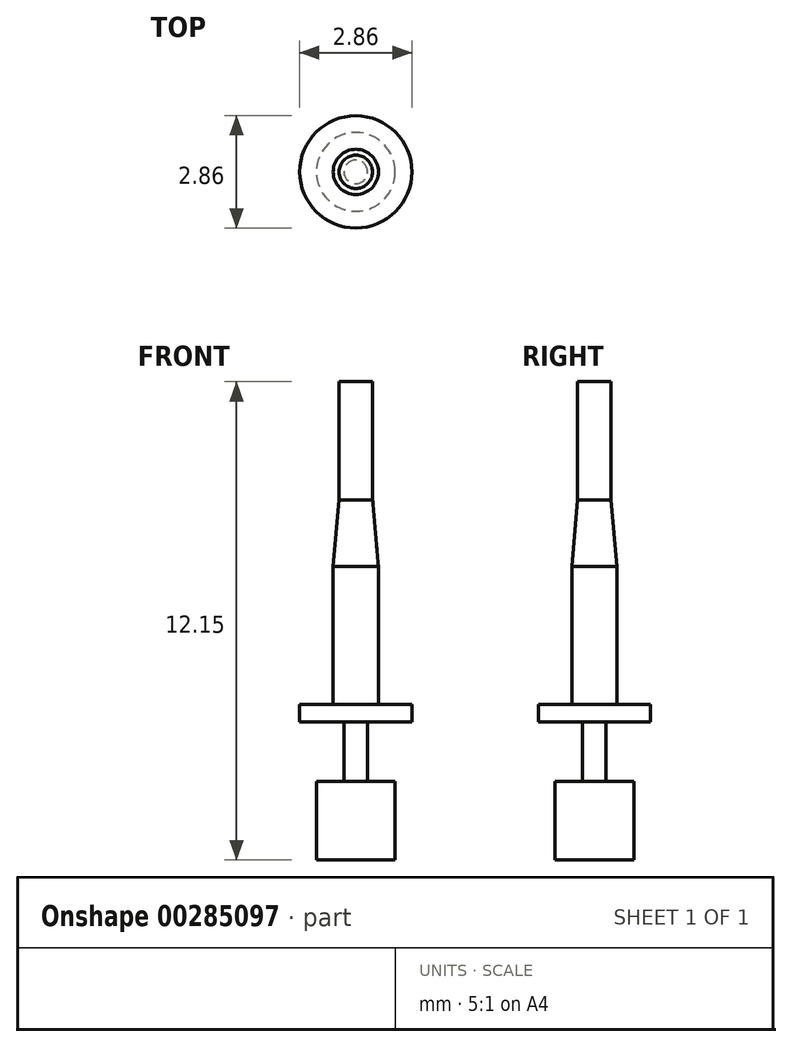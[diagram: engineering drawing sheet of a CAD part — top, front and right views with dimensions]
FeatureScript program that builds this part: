
annotation { "Feature Type Name" : "Feature", "Feature Type Description" : "" }
export const myFeature = defineFeature(function(context is Context, id is Id, definition is map)
    precondition{}
    {
        {
            var Q0;
            Q0=qCreatedBy(makeId("Top.planeOp"),FACE);
            var sketch = newSketch(context, id + "F0", { "sketchPlane" : qUnion([Q0])});
            skCircle(sketch, "E0", {"center": v(0, 0) * mm, "radius": 1 * mm});
            skSolve(sketch);
        }
        {
            var Q0;
            Q0=makeQuery(id+"F0.imprint","IMPRINT",FACE,{"disambiguationData":[TD([[makeQuery(id+"F0.imprint","IMPRINT",EDGE,{"derivedFrom":sQuery(id+"F0.wireOp",EDGE,"E0")}),1.0]])]});
            extrude(context, id + "F1", {"entities" : qUnion([Q0]), "depth" : 2 * mm});
        }
        {
            var Q0;
            Q0=makeQuery(id+"F1.opExtrude","CAP_FACE",FACE,{"disambiguationData":[OSD([sQuery(id+"F0.wireOp",EDGE,"E0")])],"isStart":false});
            var sketch = newSketch(context, id + "F2", { "sketchPlane" : qUnion([Q0])});
            skCircle(sketch, "E1", {"center": v(0, 0) * mm, "radius": 0.3 * mm});
            skSolve(sketch);
        }
        {
            var Q0;
            Q0=makeQuery(id+"F2.imprint","IMPRINT",FACE,{"disambiguationData":[TD([[makeQuery(id+"F2.imprint","IMPRINT",EDGE,{"derivedFrom":sQuery(id+"F2.wireOp",EDGE,"E1")}),1.0]])]});
            extrude(context, id + "F3", {"entities" : qUnion([Q0]), "operationType" : NewBodyOperationType.ADD, "depth" : 1.5 * mm});
        }
        {
            var Q0;
            Q0=makeQuery(id+"F3.opExtrude","CAP_FACE",FACE,{"disambiguationData":[OSD([sQuery(id+"F2.wireOp",EDGE,"E1")])],"isStart":false});
            var sketch = newSketch(context, id + "F4", { "sketchPlane" : qUnion([Q0])});
            skCircle(sketch, "E2", {"center": v(0, 0) * mm, "radius": 1.43 * mm});
            skSolve(sketch);
        }
        {
            var Q0;
            Q0=makeQuery(id+"F4.imprint","IMPRINT",FACE,{"disambiguationData":[TD([[makeQuery(id+"F4.imprint","IMPRINT",EDGE,{"derivedFrom":makeQuery(id+"F3.opExtrude","CAP_EDGE",EDGE,{"disambiguationData":[OSD([sQuery(id+"F2.wireOp",EDGE,"E1")])],"isStart":false})}),1.0]])]});
            var Q1;
            Q1=makeQuery(id+"F4.imprint","IMPRINT",FACE,{"disambiguationData":[TD([[makeQuery(id+"F4.imprint","IMPRINT",EDGE,{"derivedFrom":sQuery(id+"F4.wireOp",EDGE,"E2")}),1.0]])]});
            var Q2;
            Q2=sQuery(id+"F4.wireOp",EDGE,"E2");
            extrude(context, id + "F5", {"entities" : qUnion([Q0, Q1]), "surfaceEntities" : qUnion([Q2]), "depth" : 0.45 * mm});
        }
        {
            var Q0;
            Q0=makeQuery(id+"F5.opExtrude","CAP_FACE",FACE,{"disambiguationData":[OSD([sQuery(id+"F4.wireOp",EDGE,"E2")])],"isStart":false});
            var sketch = newSketch(context, id + "F6", { "sketchPlane" : qUnion([Q0])});
            skCircle(sketch, "E3", {"center": v(0, 0) * mm, "radius": 0.57 * mm});
            skSolve(sketch);
        }
        {
            var Q0;
            Q0=makeQuery(id+"F6.imprint","IMPRINT",FACE,{"disambiguationData":[TD([[makeQuery(id+"F6.imprint","IMPRINT",EDGE,{"derivedFrom":sQuery(id+"F6.wireOp",EDGE,"E3")}),1.0]])]});
            extrude(context, id + "F7", {"entities" : qUnion([Q0]), "operationType" : NewBodyOperationType.ADD, "depth" : 3.5 * mm});
        }
        {
            var Q0;
            Q0=makeQuery(id+"F7.opExtrude","CAP_FACE",FACE,{"disambiguationData":[OSD([sQuery(id+"F6.wireOp",EDGE,"E3")])],"isStart":false});
            var sketch = newSketch(context, id + "F8", { "sketchPlane" : qUnion([Q0])});
            skCircle(sketch, "E4", {"center": v(0, 0) * mm, "radius": 0.57 * mm});
            skSolve(sketch);
        }
        {
            var Q0;
            Q0=makeQuery(id+"F8.imprint","IMPRINT",FACE,{"disambiguationData":[TD([[makeQuery(id+"F8.imprint","IMPRINT",EDGE,{"derivedFrom":sQuery(id+"F8.wireOp",EDGE,"E4")}),1.0]])]});
            extrude(context, id + "F9", {"entities" : qUnion([Q0]), "operationType" : NewBodyOperationType.ADD, "depth" : 1.7 * mm, "hasDraft" : true, "draftAngle" : 5 * degree, "draftPullDirection" : true});
        }
        {
            var Q0;
            Q0=makeQuery(id+"F9.opExtrude","CAP_FACE",FACE,{"disambiguationData":[OSD([sQuery(id+"F8.wireOp",EDGE,"E4")])],"isStart":false});
            var sketch = newSketch(context, id + "F10", { "sketchPlane" : qUnion([Q0])});
            skCircle(sketch, "E5", {"center": v(0, 0) * mm, "radius": 0.42 * mm});
            skSolve(sketch);
        }
        {
            var Q0;
            Q0=makeQuery(id+"F10.imprint","IMPRINT",FACE,{"disambiguationData":[TD([[makeQuery(id+"F10.imprint","IMPRINT",EDGE,{"derivedFrom":sQuery(id+"F10.wireOp",EDGE,"E5")}),1.0]])]});
            extrude(context, id + "F11", {"entities" : qUnion([Q0]), "operationType" : NewBodyOperationType.ADD, "depth" : 3 * mm});
        }
    });
